# Revit family: IS_iLifeA_T5260_BIM_GB
name_source: partatom
category: Plumbing Fixtures
units: mm (PartAtom-declared; Revit-internal decimal feet)

## family parameters
Always vertical = No
Cut with Voids When Loaded = No
OmniClass Number = 23.45.05.14.21.11
OmniClass Title = Bath/Shower Units
Part Type = Normal
Room Calculation Point = No
Round Connector Dimension = Use Diameter
Shared = No
Work Plane-Based = No

## types (7) — shared parameters
Accessories = https://www.idealstandard.co.uk
AreaUnits = milliliters
BIMObjectName = IS_IdealStandard_BathroomCabinets_I.Life A_T5260
BIMobject category = Other Sanitary
BIMobject category code = other-sanitary
BIMobject main category = Sanitary
BIMobject main category code = sanitary
Brand = Ideal Standard
Brand url = http://www.idealstandard.co.uk
ConnectionType = Plumbing
CurrencyUnit = £
CurrentRevision = 1
Date of publishing = 11/03/2022
Description = I.Life A Column 2 DOORS
DurationUnit = Years
Edition number = 1
ElementType = Bathroom Furniture
Features = Column 2 DOORS
Help = https://www.idealstandard.co.uk
IFC Classification = Sanitary Terminal
IfcExportAs = IfcFurnitureType
IfcExportType = BATHROOMCABINET
Installation instructions = https://www.idealstandard.co.uk
InstallationInstructions = https://www.idealstandard.co.uk
LinearUnits = millilitres
MaintenanceInformation = https://www.idealstandard.co.uk
Manufacturer = Ideal Standard
Manufacturer name = Ideal Standard
ManufacturerURL = https://www.idealstandard.co.uk
Masterformat 2014 Code = 12 50 00
Masterformat 2014 Description = Furniture
Material = Wood
Material main = MDF
ModelReference = I.Life A Column 2 DOORS
NBS Reference Code = 45-35-72/318
NBS Reference Description = Bathroom Cabinets
Name = BathroomCabinets_I.Life A_T5260_IdealStandard
NettWeight = 30.48218508
NominalDepth = 320 mm
NominalHeight = 1600 mm  [stored 5.24934 ft]
NominalLength = 320 mm
NominalWidth = 400 mm  [stored 1.31234 ft]
OmniClass Code = 23-31 25 13
OmniClass Description = Bathroom Cabinets
PredefinedType = Bathroom Furniture
Product Guid = ad567a3f-7b05-44e6-8a01-049d44596a93
Product SKU = T5260
Product certification = https://www.idealstandard.co.uk
Product data url = https://bimobject.com
Product family = I.life
Product group = Bathroom Furniture
Product name = I.Life A Column 2 DOORS
Product url = https://www.idealstandard.co.uk
ProductInformation = https://www.idealstandard.co.uk
QR code = http://bimobject.com
Shape = rectangular
Size = 400 x 320 x 1600 mm
Space = Internal
SpareParts = https://www.idealstandard.co.uk
Technical description = https://www.idealstandard.co.uk
UNSPSC Code = 301815
URL = https://www.idealstandard.co.uk
Uniclass 1.4 Code = L8241
Uniclass 1.4 Description = Bathroom cabinets
Uniclass 2.0 Code = PR-35-75-08
Uniclass 2.0 Description = Bathroom Cabinets
Uniclass 2015 Code = Pr_40_30_78_05
Uniclass 2015 Name = Bathroom furniture
Uniclass2015Code = Pr_40_30_87_03
Uniclass2015Title = Bathroom cabinets
Uniclass2015Version = v1.25
Version = 1
VolumeUnits = Litres
WRASURL = https://www.wrasapprovals.co.uk
WarrantyDescription = manufacturer warranty
WarrantyDurationUnit = years
Youtube clip = https://www.youtube.com
zero-valued in all types: MaterialThickness

## per-type parameters (varying)
| type | BarCode | Color | Finish | GTIN code | MainColor | Model | ModelNumber |
| T5260DU - I.Life A Column 2 DOORS - Matt White | 8014140502067 | Matt White | Matt White | https://8014140502067 | Matt White | T5260DU | T5260DU |
| T5260NF - I.Life A Column 2 DOORS - Sand Beige Matt | 8014140493723 | Sand Beige Matt | Sand Beige Matt | https://8014140493723 | Sand Beige Matt | T5260NF | T5260NF |
| T5260NG - I.Life A Column 2 DOORS - Quartz Grey Matt | 8014140493730 | Quartz Grey Matt | Quartz Grey Matt | https://8014140493730 | Quartz Grey Matt | T5260NG | T5260NG |
| T5260NV - I.Life A Column 2 DOORS - Carbon Grey Matt | 8014140493754 | Carbon Grey Matt | Carbon Grey Matt | https://8014140493754 | Carbon Grey Matt | T5260NV | T5260NV |
| T5260NH - I.Life A Column 2 DOORS - Greige Matt | 8014140493747 | Greige Matt | Greige Matt | https://8014140493747 | Greige Matt | T5260NH | T5260NH |
| T5260NX - I.Life A Column 2 DOORS - Natural Oak | 8014140502081 | Natural Oak | Natural Oak | https://8014140502081 | Natural Oak | T5260NX | T5260NX |
| T5260NW - I.Life A Column 2 DOORS - Coffee Oak | 8014140502074 | Coffee Oak | Coffee Oak | https://8014140502074 | Coffee Oak | T5260NW | T5260NW |

note: [stored X ft] marks values corroborated as IEEE doubles in the binary element streams (Revit-internal decimal feet)

## geometry (parser evidence)
native form markers: Sweep x3
no freeform markers — native parametric forms only
